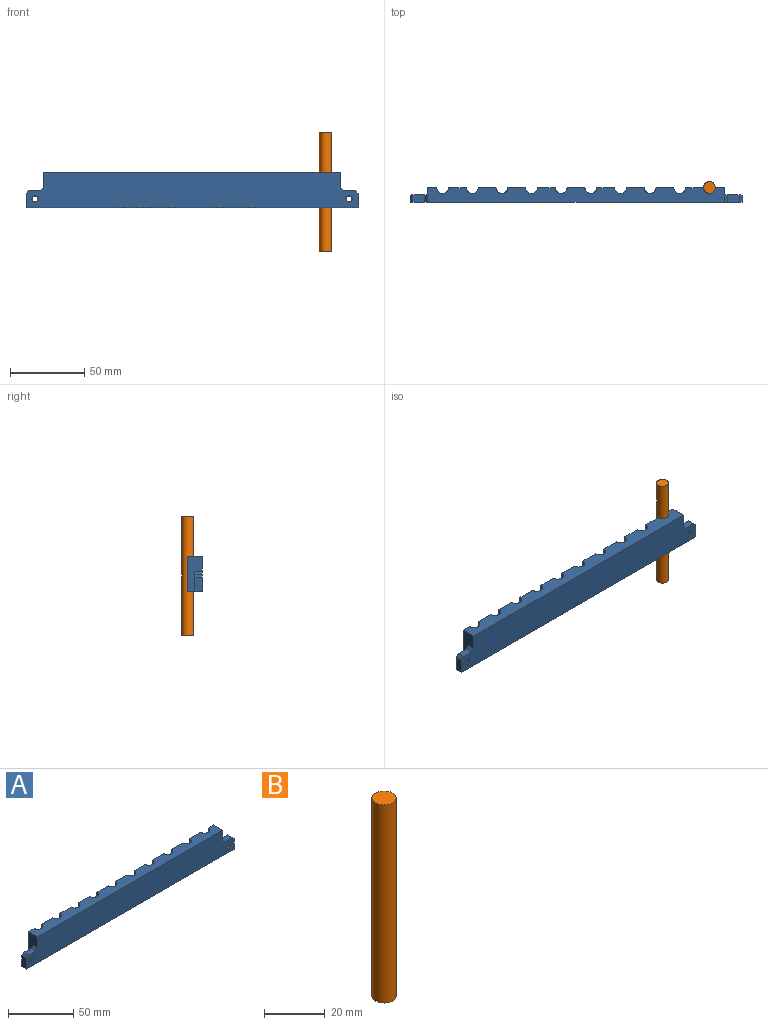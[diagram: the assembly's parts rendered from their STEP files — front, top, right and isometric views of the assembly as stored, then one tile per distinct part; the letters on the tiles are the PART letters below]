
ASSEMBLY  parts=2 mates=1
PART A: 80 faces, bbox 224x10x24 mm
  f0: plane 24x10mm, normal (-1,0,0), area 170mm2, adj f4,f5,f6,f9,f69,f75
  f1: plane 18x9mm, normal (0,0,-1), area 70.7mm2, adj f2,f4,f7,f8
  f2: plane 24x12mm, normal (0,1,0), area 168mm2, adj f1,f3,f6,f7,f8,f9,f10,f61
  f3: cylinder r=4mm len=24mm, axis (0,0,-1), area 301.6mm2, adj f2,f4,f6,f9
  f4: plane 24x6mm, normal (0,1,0), area 84mm2, adj f0,f1,f3,f6,f7,f8,f9,f10
  f5: plane 224x24mm, normal (0,-1,0), area 5062.9mm2, adj f0,f6,f9,f52,f66,f67,f68,f70
  f6: plane 200x10mm, normal (0,0,1), area 1748.7mm2, adj f0,f2,f3,f4,f5,f12,f13,f14
  f7: cylinder r=9mm len=20mm, axis (0,0,-1), area 565.5mm2, adj f1,f2,f4,f10
  f8: cylinder r=6mm len=20mm, axis (0,0,-1), area 377mm2, adj f1,f2,f4,f10
  f9: plane 224x10mm, normal (0,0,-1), area 1868.7mm2, adj f0,f2,f3,f4,f5,f12,f13,f14
  f10: plane 18x9mm, normal (0,0,1), area 70.7mm2, adj f2,f4,f7,f8
  f11: plane 18x9mm, normal (0,0,-1), area 70.7mm2, adj f12,f14,f15,f16
  f12: plane 24x12mm, normal (0,1,0), area 168mm2, adj f6,f9,f11,f13,f15,f16,f17,f18
  f13: cylinder r=4mm len=24mm, axis (0,0,-1), area 301.6mm2, adj f6,f9,f12,f14
  f14: plane 24x12mm, normal (0,1,0), area 168mm2, adj f6,f9,f11,f13,f15,f16,f17,f61
  f15: cylinder r=9mm len=20mm, axis (0,0,-1), area 565.5mm2, adj f11,f12,f14,f17
  f16: cylinder r=6mm len=20mm, axis (0,0,-1), area 377mm2, adj f11,f12,f14,f17
  f17: plane 18x9mm, normal (0,0,1), area 70.7mm2, adj f12,f14,f15,f16
  f18: plane 18x9mm, normal (0,0,-1), area 70.7mm2, adj f12,f19,f21,f22
  f19: plane 24x12mm, normal (0,1,0), area 168mm2, adj f6,f9,f18,f20,f21,f22,f23,f24
  f20: cylinder r=4mm len=24mm, axis (0,0,-1), area 301.6mm2, adj f6,f9,f12,f19
  f21: cylinder r=9mm len=20mm, axis (0,0,-1), area 565.5mm2, adj f12,f18,f19,f23
  f22: cylinder r=6mm len=20mm, axis (0,0,-1), area 377mm2, adj f12,f18,f19,f23
  f23: plane 18x9mm, normal (0,0,1), area 70.7mm2, adj f12,f19,f21,f22
  f24: plane 18x9mm, normal (0,0,-1), area 70.7mm2, adj f19,f25,f27,f28
  f25: plane 24x12mm, normal (0,1,0), area 168mm2, adj f6,f9,f24,f26,f27,f28,f29,f30
  f26: cylinder r=4mm len=24mm, axis (0,0,-1), area 301.6mm2, adj f6,f9,f19,f25
  f27: cylinder r=9mm len=20mm, axis (0,0,-1), area 565.5mm2, adj f19,f24,f25,f29
  f28: cylinder r=6mm len=20mm, axis (0,0,-1), area 377mm2, adj f19,f24,f25,f29
  f29: plane 18x9mm, normal (0,0,1), area 70.7mm2, adj f19,f25,f27,f28
  f30: plane 18x9mm, normal (0,0,-1), area 70.7mm2, adj f25,f31,f33,f34
  f31: plane 24x12mm, normal (0,1,0), area 168mm2, adj f6,f9,f30,f32,f33,f34,f35,f36
  f32: cylinder r=4mm len=24mm, axis (0,0,-1), area 301.6mm2, adj f6,f9,f25,f31
  f33: cylinder r=9mm len=20mm, axis (0,0,-1), area 565.5mm2, adj f25,f30,f31,f35
  f34: cylinder r=6mm len=20mm, axis (0,0,-1), area 377mm2, adj f25,f30,f31,f35
  f35: plane 18x9mm, normal (0,0,1), area 70.7mm2, adj f25,f31,f33,f34
  f36: plane 18x9mm, normal (0,0,-1), area 70.7mm2, adj f31,f37,f39,f40
  f37: plane 24x12mm, normal (0,1,0), area 168mm2, adj f6,f9,f36,f38,f39,f40,f41,f42
  f38: cylinder r=4mm len=24mm, axis (0,0,-1), area 301.6mm2, adj f6,f9,f31,f37
  f39: cylinder r=9mm len=20mm, axis (0,0,-1), area 565.5mm2, adj f31,f36,f37,f41
  f40: cylinder r=6mm len=20mm, axis (0,0,-1), area 377mm2, adj f31,f36,f37,f41
  f41: plane 18x9mm, normal (0,0,1), area 70.7mm2, adj f31,f37,f39,f40
  f42: plane 18x9mm, normal (0,0,-1), area 70.7mm2, adj f37,f43,f45,f46
  f43: plane 24x12mm, normal (0,1,0), area 168mm2, adj f6,f9,f42,f44,f45,f46,f47,f56
  f44: cylinder r=4mm len=24mm, axis (0,0,-1), area 301.6mm2, adj f6,f9,f37,f43
  f45: cylinder r=9mm len=20mm, axis (0,0,-1), area 565.5mm2, adj f37,f42,f43,f47
  f46: cylinder r=6mm len=20mm, axis (0,0,-1), area 377mm2, adj f37,f42,f43,f47
  f47: plane 18x9mm, normal (0,0,1), area 70.7mm2, adj f37,f43,f45,f46
  f48: plane 18x9mm, normal (0,0,-1), area 70.7mm2, adj f49,f51,f53,f54
  f49: plane 24x6mm, normal (0,1,0), area 84mm2, adj f6,f9,f48,f50,f52,f53,f54,f55
  f50: cylinder r=4mm len=24mm, axis (0,0,-1), area 301.6mm2, adj f6,f9,f49,f51
  f51: plane 24x12mm, normal (0,1,0), area 168mm2, adj f6,f9,f48,f50,f53,f54,f55,f56
  f52: plane 24x10mm, normal (1,0,0), area 170mm2, adj f5,f6,f9,f49,f73,f76
  f53: cylinder r=9mm len=20mm, axis (0,0,-1), area 565.5mm2, adj f48,f49,f51,f55
  f54: cylinder r=6mm len=20mm, axis (0,0,-1), area 377mm2, adj f48,f49,f51,f55
  f55: plane 18x9mm, normal (0,0,1), area 70.7mm2, adj f49,f51,f53,f54
  f56: plane 18x9mm, normal (0,0,-1), area 70.7mm2, adj f43,f51,f58,f59
  f57: cylinder r=4mm len=24mm, axis (0,0,-1), area 301.6mm2, adj f6,f9,f43,f51
  f58: cylinder r=9mm len=20mm, axis (0,0,-1), area 565.5mm2, adj f43,f51,f56,f60
  f59: cylinder r=6mm len=20mm, axis (0,0,-1), area 377mm2, adj f43,f51,f56,f60
  f60: plane 18x9mm, normal (0,0,1), area 70.7mm2, adj f43,f51,f58,f59
  f61: plane 18x9mm, normal (0,0,-1), area 70.7mm2, adj f2,f14,f63,f64
  f62: cylinder r=4mm len=24mm, axis (0,0,-1), area 301.6mm2, adj f2,f6,f9,f14
  f63: cylinder r=9mm len=20mm, axis (0,0,-1), area 565.5mm2, adj f2,f14,f61,f65
  f64: cylinder r=6mm len=20mm, axis (0,0,-1), area 377mm2, adj f2,f14,f61,f65
  f65: plane 18x9mm, normal (0,0,1), area 70.7mm2, adj f2,f14,f63,f64
  f66: plane 8x5mm, normal (0,0,1), area 40mm2, adj f5,f69,f74,f75
  f67: plane 10x5mm, normal (-1,0,0), area 50mm2, adj f5,f9,f69,f74
  f68: cylinder r=2mm len=4mm, axis (0,-1,0), area 25.1mm2, adj f5,f79
  f69: plane 14x12mm, normal (0,1,0), area 65.5mm2, adj f0,f9,f66,f67,f74,f75,f79
  f70: plane 10x5mm, normal (1,0,0), area 50mm2, adj f5,f9,f73,f77
  f71: plane 8x5mm, normal (0,0,1), area 40mm2, adj f5,f73,f76,f77
  f72: cylinder r=2mm len=4mm, axis (0,-1,0), area 25.1mm2, adj f5,f78
  f73: plane 14x12mm, normal (0,1,0), area 65.5mm2, adj f9,f52,f70,f71,f76,f77,f78
  f74: plane 5x2mm, normal (-0.71,0,0.71), area 14.1mm2, adj f5,f66,f67,f69
  f75: plane 5x2mm, normal (-0.71,0,0.71), area 14.1mm2, adj f0,f5,f66,f69
  f76: plane 5x2mm, normal (0.71,0,0.71), area 14.1mm2, adj f5,f52,f71,f73
  f77: plane 5x2mm, normal (0.71,0,0.71), area 14.1mm2, adj f5,f70,f71,f73
  f78: cone r=2mm half-angle=45deg, axis (0,1,0), area 93.3mm2, adj f72,f73
  f79: cone r=5mm half-angle=45deg, axis (0,1,0), area 93.3mm2, adj f68,f69
PART B: 3 faces, bbox 8x8x80 mm
  f0: cylinder r=4mm len=80mm, axis (0,0,-1), area 2010.6mm2, adj f1,f2
  f1: plane 8x8mm, normal (0,0,1), area 50.3mm2, adj f0
  f2: plane 8x8mm, normal (0,0,-1), area 50.3mm2, adj f0
PLACE A t=(4.36,-7.45,0)mm fixed
PLACE B t=(184.36,2.55,-41.32)mm
MATE slider B.f0 <-> A.f50  axis (0,0,1) through (184.36,2.55,-1.32)mm
